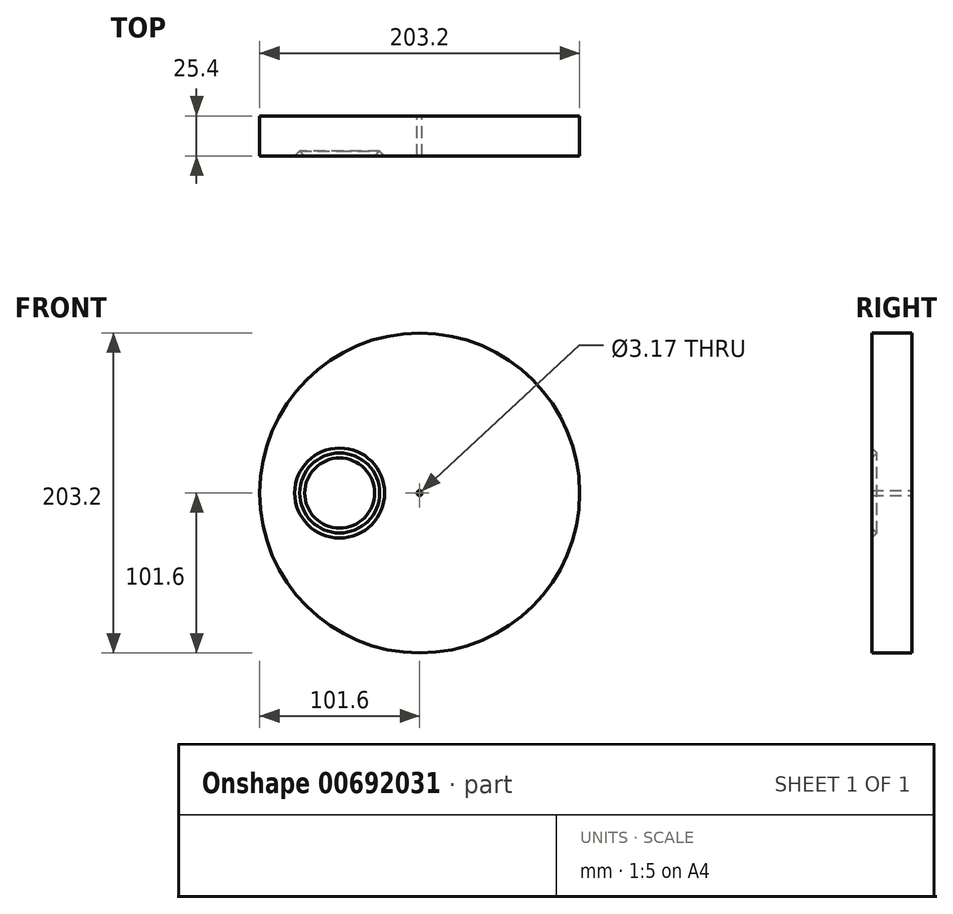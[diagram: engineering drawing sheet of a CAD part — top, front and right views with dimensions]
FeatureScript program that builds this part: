
annotation { "Feature Type Name" : "Feature", "Feature Type Description" : "" }
export const myFeature = defineFeature(function(context is Context, id is Id, definition is map)
    precondition{}
    {
        {
            var Q0;
            Q0=qCreatedBy(makeId("Front.planeOp"),FACE);
            var sketch = newSketch(context, id + "F0", { "sketchPlane" : qUnion([Q0])});
            skCircle(sketch, "E0", {"center": v(0, 0) * mm, "radius": 101.6 * mm});
            skCircle(sketch, "E1", {"center": v(0, 0) * mm, "radius": 1.59 * mm});
            skLineSegment(sketch, "E2", {"start": v(-1.59, 16.44) * mm, "end": v(-1.59, -14.53) * mm, "construction": true});
            skSolve(sketch);
        }
        {
            var Q0;
            Q0=makeQuery(id+"F0.imprint","IMPRINT",FACE,{"disambiguationData":[TD([[makeQuery(id+"F0.imprint","IMPRINT",EDGE,{"derivedFrom":sQuery(id+"F0.wireOp",EDGE,"E0")}),1.0]])]});
            extrude(context, id + "F1", {"entities" : qUnion([Q0]), "depth" : 25.4 * mm, "offsetDistance" : 25.4 * mm});
        }
        {
            var Q0;
            Q0=qCreatedBy(makeId("Top.planeOp"),FACE);
            var sketch = newSketch(context, id + "F2", { "sketchPlane" : qUnion([Q0])});
            skLineSegment(sketch, "E3", {"start": v(1.59, 0) * mm, "end": v(1.59, -25.4) * mm});
            skLineSegment(sketch, "E4", {"start": v(0, 17.87) * mm, "end": v(0, -41.02) * mm, "construction": true});
            skLineSegment(sketch, "E5", {"start": v(-73.02, -25.4) * mm, "end": v(-76.2, -22.22) * mm});
            skLineSegment(sketch, "E6", {"start": v(-76.2, -22.23) * mm, "end": v(-79.37, -25.4) * mm});
            skLineSegment(sketch, "E7", {"start": v(-79.37, -25.4) * mm, "end": v(-73.02, -25.4) * mm});
            skLineSegment(sketch, "E8", {"start": v(-1.59, -25.4) * mm, "end": v(-1.59, 0) * mm});
            skLineSegment(sketch, "E9", {"start": v(-50.8, 0) * mm, "end": v(-50.8, -25.4) * mm, "construction": true});
            skLineSegment(sketch, "E10", {"start": v(101.6, 0) * mm, "end": v(101.6, -25.4) * mm});
            skLineSegment(sketch, "E11", {"start": v(-101.6, -25.4) * mm, "end": v(-101.6, 0) * mm});
            skSolve(sketch);
        }
        {
            var Q0;
            Q0 = qSketchRegion(id + "F2", true);
            var Q1;
            Q1=sQuery(id+"F2.wireOp",EDGE,"E9");
            revolve(context, id + "F3", {"operationType" : NewBodyOperationType.REMOVE, "entities" : qUnion([Q0]), "axis" : qUnion([Q1]), "revolveType" : RevolveType.FULL, "oppositeDirection" : true});
        }
    });
